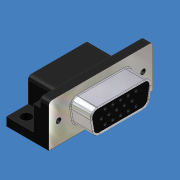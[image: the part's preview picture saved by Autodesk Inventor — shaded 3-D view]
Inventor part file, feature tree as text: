
AUTODESK INVENTOR PART (.ipt)
format: ipt  version: unknown  size: 355,328 bytes
history: native  units: mm (DEFAULTED — no unit token found)
features: sketch x7, extrude x5, fillet x2, hole x2, pattern_linear x1
ambient origin geometry x8: Origin, YZ Plane, XZ Plane, XY Plane, X Axis, Y Axis, Z Axis, Center Point
feature tree (17):
  extrude  "Extrusion1"  Depth=12.5mm
  extrude  "Extrusion4"  Depth=17.453293mm
  extrude  "Extrusion2"  Depth=16.92mm
  fillet  "Fillet1"  Radius=0.5mm
  hole  "Hole1"  [1 undecoded]
  extrude  "Extrusion3"  Depth=1.98mm
  pattern_linear  "Rectangular Pattern1"  Spacing1=0.5mm  [1 undecoded]
  fillet  "Fillet3"  Radius=0.76mm
  hole  "Hole2"  [1 undecoded]
  extrude  "Extrusion5"  Depth=2.75mm
  sketch  "Sketch1"  dims[d4=12.5mm d5=12.5mm]
  sketch  "Sketch2"  dims[d6=30.8mm d7=0.0mm d9=17.453293mm]
  sketch  "Sketch3"  dims[d11=1.5mm d12=16.92mm d13=0.5mm]
  sketch  "Sketch4"  dims[d14=6.1mm d15=0.0mm d16=0.25mm]
  sketch  "Sketch6"  dims[d17=25.0mm]
  sketch  "Sketch7"  dims[d18=1.5mm d19=6.0mm d20=4.0mm d21=2.0mm d22=14.3117mm d23=8.0mm d24=20.594885mm d27=1.98mm]
  sketch  "Sketch8"  dims[d28=4.56mm d29=0.5mm d30=0.0mm d31=0.76mm d33=100.0mm d35=1.14mm d36=30.0mm d38=1.98mm d40=2.75mm d41=2.5mm d42=18.0mm d43=2.0mm d44=7.25mm d45=0.0mm d46=1.0mm d47=9.525mm d48=25.0mm d49=3.0mm d50=6.0mm d51=4.0mm d52=2.0mm d53=14.3117mm d54=8.0mm d55=20.594885mm d56=7.3mm d57=5.85mm d58=0.0mm]
note: 3 required parameter values undecoded (feature->parameter linkage not recoverable at this tier; creation-order binding heuristic only, values carry confidence <= 0.55)
